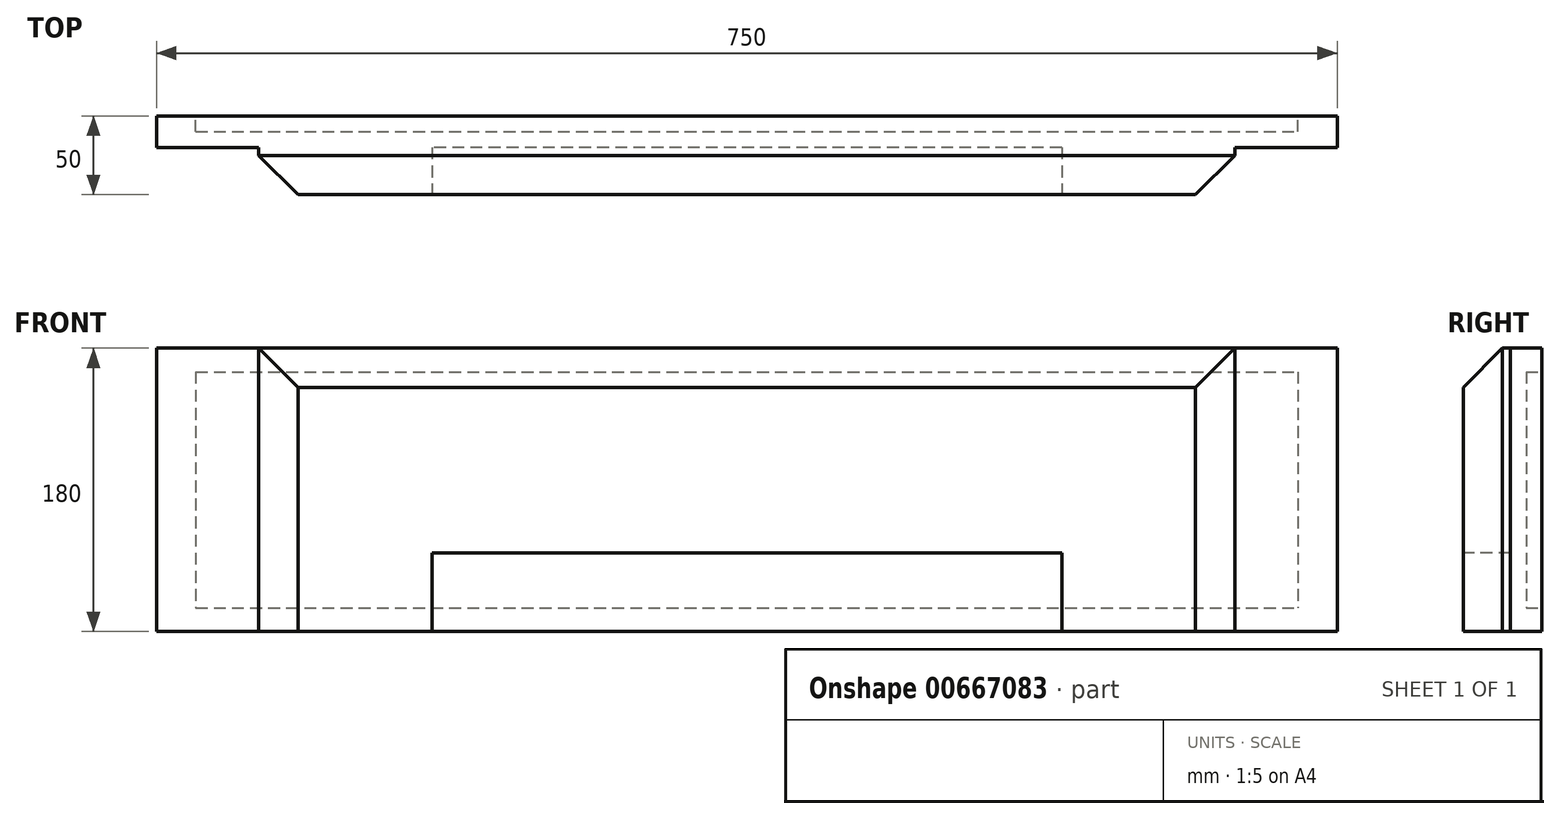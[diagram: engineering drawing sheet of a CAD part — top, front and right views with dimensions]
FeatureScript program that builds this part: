
annotation { "Feature Type Name" : "Feature", "Feature Type Description" : "" }
export const myFeature = defineFeature(function(context is Context, id is Id, definition is map)
    precondition{}
    {
        {
            var Q0;
            Q0=qCreatedBy(makeId("Front.planeOp"),FACE);
            var sketch = newSketch(context, id + "F0", { "sketchPlane" : qUnion([Q0])});
            skLineSegment(sketch, "E0.bottom", {"start": v(375, 90) * mm, "end": v(-375, 90) * mm});
            skLineSegment(sketch, "E0.top", {"start": v(375, -90) * mm, "end": v(-375, -90) * mm});
            skLineSegment(sketch, "E0.left", {"start": v(375, 90) * mm, "end": v(375, -90) * mm});
            skLineSegment(sketch, "E0.right", {"start": v(-375, 90) * mm, "end": v(-375, -90) * mm});
            skPoint(sketch, "E0.middle", {"position": v(0, 0) * mm});
            skSolve(sketch);
        }
        {
            var Q0;
            Q0=makeQuery(id+"F0.imprint","IMPRINT",FACE,{"disambiguationData":[TD([[makeQuery(id+"F0.imprint","IMPRINT",EDGE,{"derivedFrom":sQuery(id+"F0.wireOp",EDGE,"E0.bottom")}),1.0]])]});
            extrude(context, id + "F1", {"entities" : qUnion([Q0]), "depth" : 20 * mm, "offsetDistance" : 25 * mm});
        }
        {
            var Q0;
            Q0=makeQuery(id+"F1.opExtrude","CAP_FACE",FACE,{"disambiguationData":[OSD([sQuery(id+"F0.wireOp",EDGE,"E0.bottom"),sQuery(id+"F0.wireOp",EDGE,"E0.top"),sQuery(id+"F0.wireOp",EDGE,"E0.left"),sQuery(id+"F0.wireOp",EDGE,"E0.right")])],"isStart":false});
            var sketch = newSketch(context, id + "F2", { "sketchPlane" : qUnion([Q0])});
            skLineSegment(sketch, "E1.bottom", {"start": v(310, 90) * mm, "end": v(-310, 90) * mm});
            skLineSegment(sketch, "E1.top", {"start": v(310, -90) * mm, "end": v(-310, -90) * mm});
            skLineSegment(sketch, "E1.left", {"start": v(310, 90) * mm, "end": v(310, -90) * mm});
            skLineSegment(sketch, "E1.right", {"start": v(-310, 90) * mm, "end": v(-310, -90) * mm});
            skPoint(sketch, "E1.middle", {"position": v(0, 0) * mm});
            skSolve(sketch);
        }
        {
            var Q0;
            Q0=makeQuery(id+"F2.imprint","IMPRINT",FACE,{"disambiguationData":[TD([[makeQuery(id+"F2.imprint","IMPRINT",EDGE,{"derivedFrom":sQuery(id+"F2.wireOp",EDGE,"E1.bottom")}),1.0]])]});
            extrude(context, id + "F3", {"entities" : qUnion([Q0]), "operationType" : NewBodyOperationType.ADD, "depth" : 30 * mm, "offsetDistance" : 25 * mm});
        }
        {
            var Q0;
            Q0=makeQuery(id+"F3.opExtrude","CAP_EDGE",EDGE,{"disambiguationData":[OSD([sQuery(id+"F2.wireOp",EDGE,"E1.bottom")])],"isStart":false});
            var Q1;
            Q1=makeQuery(id+"F3.opExtrude","CAP_EDGE",EDGE,{"disambiguationData":[OSD([sQuery(id+"F2.wireOp",EDGE,"E1.right")])],"isStart":false});
            var Q2;
            Q2=makeQuery(id+"F3.opExtrude","CAP_EDGE",EDGE,{"disambiguationData":[OSD([sQuery(id+"F2.wireOp",EDGE,"E1.left")])],"isStart":false});
            chamfer(context, id + "F4", {"entities" : qUnion([Q0, Q1, Q2]), "width" : 25 * mm, "tangentPropagation" : true});
        }
        {
            var Q0;
            Q0=makeQuery(id+"F3.opExtrude","CAP_FACE",FACE,{"disambiguationData":[OSD([sQuery(id+"F2.wireOp",EDGE,"E1.bottom"),sQuery(id+"F2.wireOp",EDGE,"E1.top"),sQuery(id+"F2.wireOp",EDGE,"E1.left"),sQuery(id+"F2.wireOp",EDGE,"E1.right")])],"isStart":false});
            var sketch = newSketch(context, id + "F5", { "sketchPlane" : qUnion([Q0])});
            skLineSegment(sketch, "E2.bottom", {"start": v(-200, -90) * mm, "end": v(200, -90) * mm});
            skLineSegment(sketch, "E2.top", {"start": v(-200, -40) * mm, "end": v(200, -40) * mm});
            skLineSegment(sketch, "E2.left", {"start": v(-200, -90) * mm, "end": v(-200, -40) * mm});
            skLineSegment(sketch, "E2.right", {"start": v(200, -90) * mm, "end": v(200, -40) * mm});
            skSolve(sketch);
        }
        {
            var Q0;
            Q0=makeQuery(id+"F5.imprint","IMPRINT",FACE,{"disambiguationData":[TD([[makeQuery(id+"F5.imprint","IMPRINT",EDGE,{"derivedFrom":sQuery(id+"F5.wireOp",EDGE,"E2.bottom")}),-1.0]])]});
            extrude(context, id + "F6", {"entities" : qUnion([Q0]), "operationType" : NewBodyOperationType.REMOVE, "oppositeDirection" : true, "depth" : 30 * mm, "offsetDistance" : 25 * mm});
        }
        {
            var Q0;
            Q0=makeQuery(id+"F1.opExtrude","CAP_FACE",FACE,{"disambiguationData":[OSD([sQuery(id+"F0.wireOp",EDGE,"E0.bottom"),sQuery(id+"F0.wireOp",EDGE,"E0.top"),sQuery(id+"F0.wireOp",EDGE,"E0.left"),sQuery(id+"F0.wireOp",EDGE,"E0.right")])],"isStart":true});
            var sketch = newSketch(context, id + "F7", { "sketchPlane" : qUnion([Q0])});
            skLineSegment(sketch, "E3.bottom", {"start": v(350, 75) * mm, "end": v(-350, 75) * mm});
            skLineSegment(sketch, "E3.top", {"start": v(350, -75) * mm, "end": v(-350, -75) * mm});
            skLineSegment(sketch, "E3.left", {"start": v(350, 75) * mm, "end": v(350, -75) * mm});
            skLineSegment(sketch, "E3.right", {"start": v(-350, 75) * mm, "end": v(-350, -75) * mm});
            skPoint(sketch, "E3.middle", {"position": v(0, 0) * mm});
            skSolve(sketch);
        }
        {
            var Q0;
            Q0=makeQuery(id+"F7.imprint","IMPRINT",FACE,{"disambiguationData":[TD([[makeQuery(id+"F7.imprint","IMPRINT",EDGE,{"derivedFrom":sQuery(id+"F7.wireOp",EDGE,"E3.bottom")}),1.0]])]});
            extrude(context, id + "F8", {"entities" : qUnion([Q0]), "operationType" : NewBodyOperationType.REMOVE, "oppositeDirection" : true, "depth" : 10 * mm, "offsetDistance" : 25 * mm});
        }
    });
